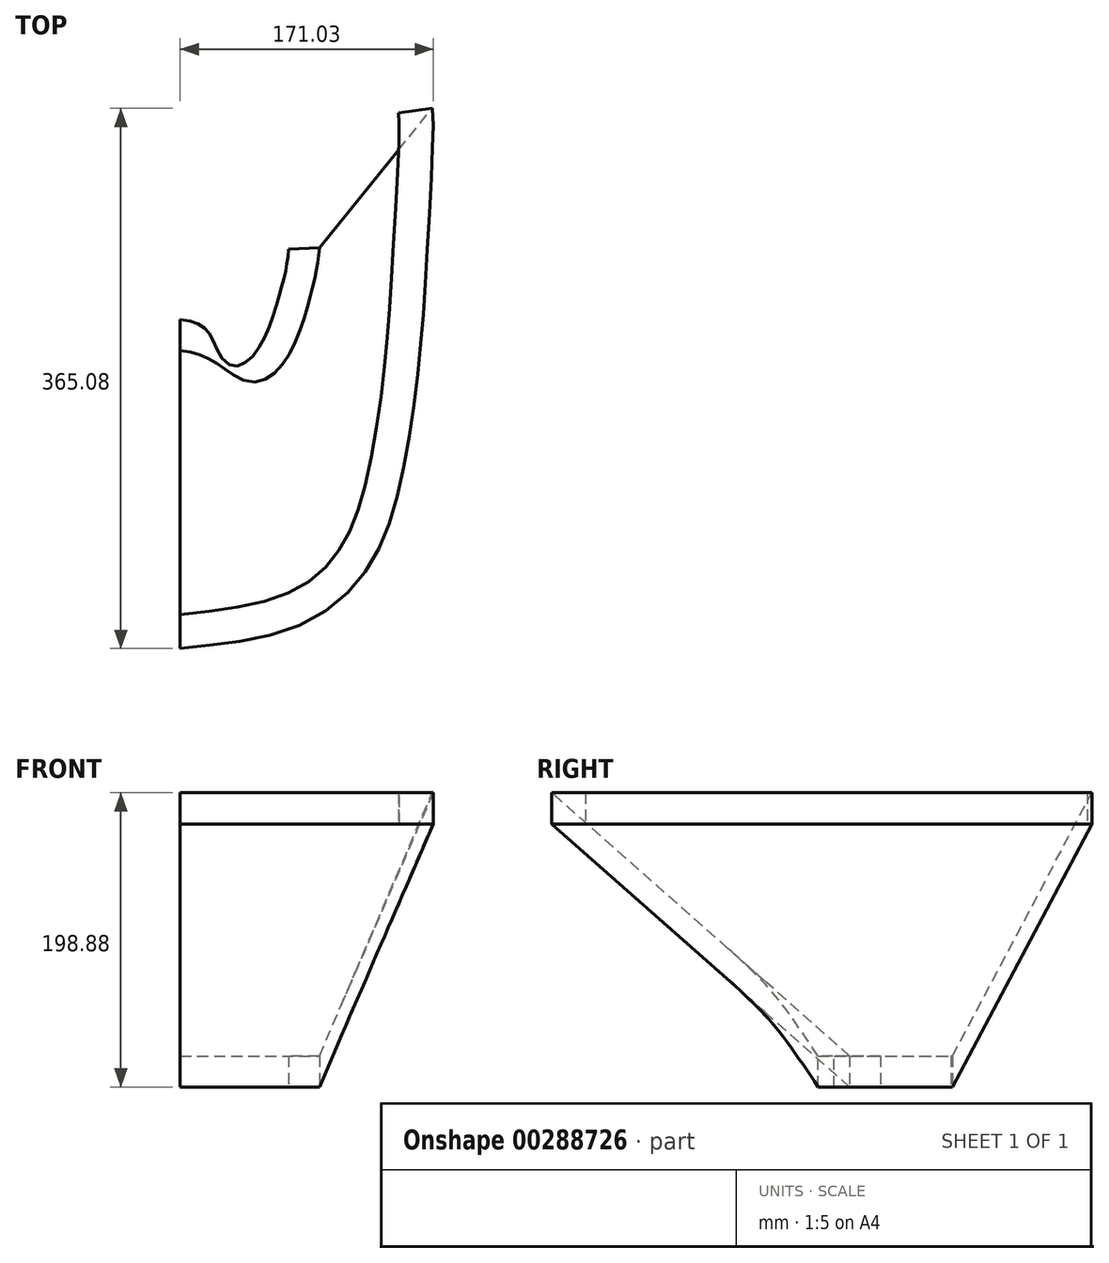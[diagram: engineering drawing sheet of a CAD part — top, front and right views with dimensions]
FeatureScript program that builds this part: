
annotation { "Feature Type Name" : "Feature", "Feature Type Description" : "" }
export const myFeature = defineFeature(function(context is Context, id is Id, definition is map)
    precondition{}
    {
        {
            var Q0;
            Q0=qCreatedBy(makeId("Top.planeOp"),FACE);
            var sketch = newSketch(context, id + "F0", { "sketchPlane" : qUnion([Q0])});
            skFitSpline(sketch, "E0", {"points": [v(0, -142.04) * mm, v(66.93, -129.6) * mm, v(97.2, -106.39) * mm, v(114.35, -68.72) * mm, v(128.48, 11) * mm, v(135.2, 98.44) * mm, v(139.01, 182.75) * mm, v(138.54, 186.55) * mm], "startDerivative": vector(449.47, 47.21) * mm, "endDerivative": vector(-15.33, 62.01) * mm});
            skSolve(sketch);
        }
        {
            var Q0;
            Q0=qCreatedBy(makeId("Right.planeOp"),FACE);
            var sketch = newSketch(context, id + "F1", { "sketchPlane" : qUnion([Q0])});
            skLineSegment(sketch, "E1.bottom", {"start": v(-174.12, 9.47) * mm, "end": v(-151.07, 9.47) * mm});
            skLineSegment(sketch, "E1.top", {"start": v(-174.12, -11.73) * mm, "end": v(-151.07, -11.73) * mm});
            skLineSegment(sketch, "E1.left", {"start": v(-174.12, 9.47) * mm, "end": v(-174.12, -11.73) * mm});
            skLineSegment(sketch, "E1.right", {"start": v(-151.07, 9.47) * mm, "end": v(-151.07, -11.73) * mm});
            skSolve(sketch);
        }
        {
            var Q0;
            Q0=makeQuery(id+"F1.imprint","IMPRINT",FACE,{"disambiguationData":[TD([[makeQuery(id+"F1.imprint","IMPRINT",EDGE,{"derivedFrom":sQuery(id+"F1.wireOp",EDGE,"E1.bottom")}),-1.0]])]});
            var Q1;
            Q1=sQuery(id+"F0.wireOp",EDGE,"E0");
            sweep(context, id + "F2", {"profiles" : qUnion([Q0]), "path" : qUnion([Q1])});
        }
        {
            var Q0;
            Q0=qCreatedBy(makeId("Right.planeOp"),FACE);
            var sketch = newSketch(context, id + "F3", { "sketchPlane" : qUnion([Q0])});
            skLineSegment(sketch, "E2.bottom", {"start": v(27.35, -168.5) * mm, "end": v(48.25, -168.5) * mm});
            skLineSegment(sketch, "E2.top", {"start": v(27.35, -189.4) * mm, "end": v(48.25, -189.4) * mm});
            skLineSegment(sketch, "E2.left", {"start": v(27.35, -168.5) * mm, "end": v(27.35, -189.4) * mm});
            skLineSegment(sketch, "E2.right", {"start": v(48.25, -168.5) * mm, "end": v(48.25, -189.4) * mm});
            skSolve(sketch);
        }
        {
            var Q0;
            Q0=qCreatedBy(makeId("Top.planeOp"),FACE);
            var sketch = newSketch(context, id + "F4", { "sketchPlane" : qUnion([Q0])});
            skFitSpline(sketch, "E3", {"points": [v(30.47, 11.6) * mm, v(76.61, 18.36) * mm, v(104.09, 88.84) * mm, v(108.2, 128.18) * mm], "startDerivative": vector(162.4, -18.38) * mm, "endDerivative": vector(6.79, 117.32) * mm});
            skSolve(sketch);
        }
        {
            var Q0;
            Q0=makeQuery(id+"F3.imprint","IMPRINT",FACE,{"disambiguationData":[TD([[makeQuery(id+"F3.imprint","IMPRINT",EDGE,{"derivedFrom":sQuery(id+"F3.wireOp",EDGE,"E2.bottom")}),-1.0]])]});
            var Q1;
            Q1=sQuery(id+"F4.wireOp",EDGE,"E3");
            sweep(context, id + "F5", {"profiles" : qUnion([Q0]), "path" : qUnion([Q1])});
        }
        {
            var Q0;
            Q0=makeQuery(id+"F5.opSweep","SWEPT_FACE",FACE,{"disambiguationData":[OSD([sQuery(id+"F3.wireOp",EDGE,"E2.left"),sQuery(id+"F4.wireOp",EDGE,"E3")])]});
            var Q1;
            Q1=makeQuery(id+"F2.opSweep","SWEPT_FACE",FACE,{"disambiguationData":[OSD([sQuery(id+"F0.wireOp",EDGE,"E0"),sQuery(id+"F1.wireOp",EDGE,"E1.left")])]});
            loft(context, id + "F6", {"sheetProfilesArray" : [{ "sheetProfileEntities" : qUnion([Q0]) }, { "sheetProfileEntities" : qUnion([Q1]) }]});
        }
    });
